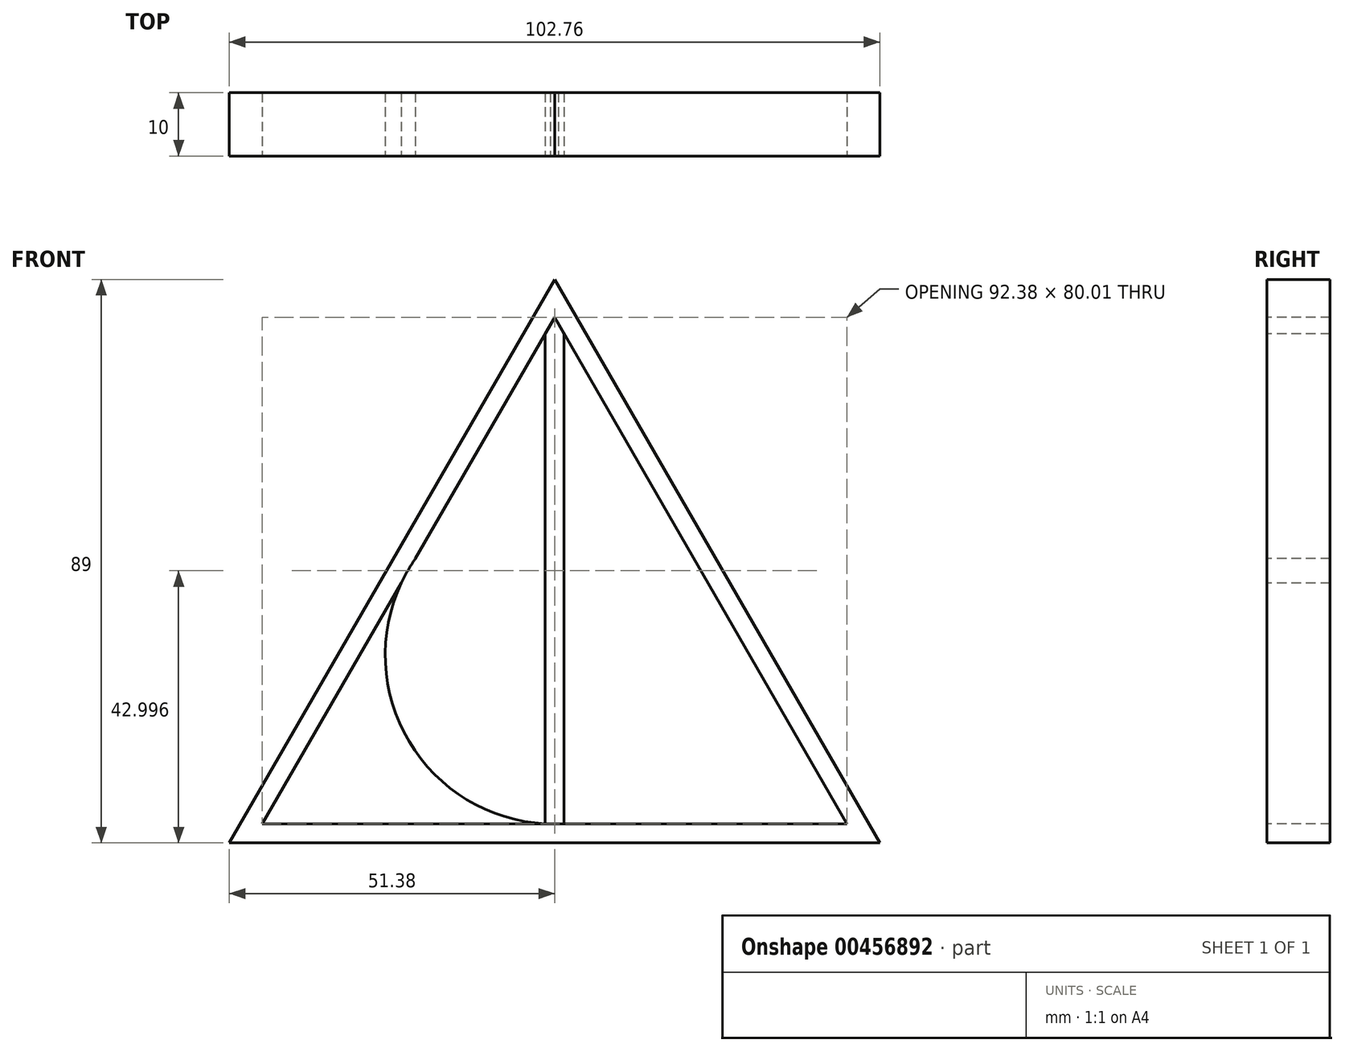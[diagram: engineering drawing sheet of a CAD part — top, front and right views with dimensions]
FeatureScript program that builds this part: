
annotation { "Feature Type Name" : "Feature", "Feature Type Description" : "" }
export const myFeature = defineFeature(function(context is Context, id is Id, definition is map)
    precondition{}
    {
        {
            var Q0;
            Q0=qCreatedBy(makeId("Front.planeOp"),FACE);
            var sketch = newSketch(context, id + "F0", { "sketchPlane" : qUnion([Q0])});
            skLineSegment(sketch, "E0", {"start": v(-46.19, 0) * mm, "end": v(46.19, 0) * mm});
            skLineSegment(sketch, "E1", {"start": v(46.19, 0) * mm, "end": v(0, 80) * mm});
            skLineSegment(sketch, "E2", {"start": v(0, 80) * mm, "end": v(-46.19, 0) * mm});
            skCircle(sketch, "E3", {"center": v(-0.05, 26.7) * mm, "radius": 26.7 * mm});
            skPoint(sketch, "E3.second.point", {"position": v(0, 53.4) * mm});
            skPoint(sketch, "E3.third.point", {"position": v(9.46, 51.64) * mm});
            skCircle(sketch, "E4", {"center": v(-0.05, 26.7) * mm, "radius": 24.15 * mm});
            skLineSegment(sketch, "E5", {"start": v(0, 86) * mm, "end": v(-51.38, -3) * mm});
            skLineSegment(sketch, "E6", {"start": v(-51.38, -3) * mm, "end": v(51.38, -3) * mm});
            skLineSegment(sketch, "E7", {"start": v(51.38, -3) * mm, "end": v(0, 86) * mm});
            skLineSegment(sketch, "E8", {"start": v(-1.5, 77.4) * mm, "end": v(-1.5, 0) * mm});
            skLineSegment(sketch, "E9.MirrorCS", {"start": v(1.5, 77.4) * mm, "end": v(1.5, 0) * mm});
            skSolve(sketch);
        }
        {
            var Q0;
            {var subQ0=sQuery(id+"F0.wireOp",EDGE,"E2");var subQ1=sQuery(id+"F0.wireOp",EDGE,"E1");var subQ2=makeQuery(id+"F0.imprint","INTERSECT",VERTEX,{"derivedFrom":[subQ1,subQ0]});Q0=makeQuery(id+"F0.imprint","IMPRINT",FACE,{"disambiguationData":[TD([[makeQuery(id+"F0.imprint","IMPRINT",EDGE,{"disambiguationData":[TD([[subQ2,1.0]])],"derivedFrom":subQ1}),1.0]])]});}
            var Q1;
            {var subQ0=sQuery(id+"F0.wireOp",EDGE,"E8");var subQ1=sQuery(id+"F0.wireOp",EDGE,"E3");var subQ2=makeQuery(id+"F0.imprint","INTERSECT",VERTEX,{"disambiguationData":[OD(0.0)],"derivedFrom":[subQ1,subQ0]});Q1=makeQuery(id+"F0.imprint","IMPRINT",FACE,{"disambiguationData":[TD([[makeQuery(id+"F0.imprint","IMPRINT",EDGE,{"disambiguationData":[TD([[subQ2,1.0]])],"derivedFrom":subQ1}),1.0]])]});}
            var Q2;
            {var subQ0=sQuery(id+"F0.wireOp",EDGE,"E8");var subQ1=sQuery(id+"F0.wireOp",EDGE,"E4");var subQ2=makeQuery(id+"F0.imprint","INTERSECT",VERTEX,{"disambiguationData":[OD(0.0)],"derivedFrom":[subQ1,subQ0]});Q2=makeQuery(id+"F0.imprint","IMPRINT",FACE,{"disambiguationData":[TD([[makeQuery(id+"F0.imprint","IMPRINT",EDGE,{"disambiguationData":[TD([[subQ2,1.0]])],"derivedFrom":subQ1}),1.0]])]});}
            var Q3;
            {var subQ5=sQuery(id+"F0.wireOp",EDGE,"E3");var subQ6=sQuery(id+"F0.wireOp",EDGE,"E0");var subQ7=makeQuery(id+"F0.imprint","INTERSECT",VERTEX,{"disambiguationData":[OD(0.0)],"derivedFrom":[subQ6,subQ5]});Q3=makeQuery(id+"F0.imprint","IMPRINT",FACE,{"disambiguationData":[TD([[makeQuery(id+"F0.imprint","IMPRINT",EDGE,{"disambiguationData":[TD([[subQ7,-1.0]])],"derivedFrom":subQ6}),1.0]])]});}
            var Q4;
            {var subQ0=sQuery(id+"F0.wireOp",EDGE,"E9.MirrorCS");var subQ1=sQuery(id+"F0.wireOp",EDGE,"E3");var subQ2=makeQuery(id+"F0.imprint","INTERSECT",VERTEX,{"disambiguationData":[OD(0.0)],"derivedFrom":[subQ1,subQ0]});Q4=makeQuery(id+"F0.imprint","IMPRINT",FACE,{"disambiguationData":[TD([[makeQuery(id+"F0.imprint","IMPRINT",EDGE,{"disambiguationData":[TD([[subQ2,1.0]])],"derivedFrom":subQ1}),1.0]])]});}
            var Q5;
            {var subQ4=sQuery(id+"F0.wireOp",EDGE,"E3");var subQ5=sQuery(id+"F0.wireOp",EDGE,"E2");var subQ6=makeQuery(id+"F0.imprint","INTERSECT",VERTEX,{"disambiguationData":[OD(0.0)],"derivedFrom":[subQ5,subQ4]});Q5=makeQuery(id+"F0.imprint","IMPRINT",FACE,{"disambiguationData":[TD([[makeQuery(id+"F0.imprint","IMPRINT",EDGE,{"disambiguationData":[TD([[subQ6,-1.0]])],"derivedFrom":subQ5}),1.0]])]});}
            extrude(context, id + "F1", {"entities" : qUnion([Q0, Q1, Q2, Q3, Q4, Q5]), "oppositeDirection" : true, "depth" : 10 * mm});
        }
        {
            var Q0;
            Q0 = qSketchRegion(id + "F0", true);
            extrude(context, id + "F2", {"entities" : qUnion([Q0]), "oppositeDirection" : true, "depth" : 10 * mm});
        }
    });
